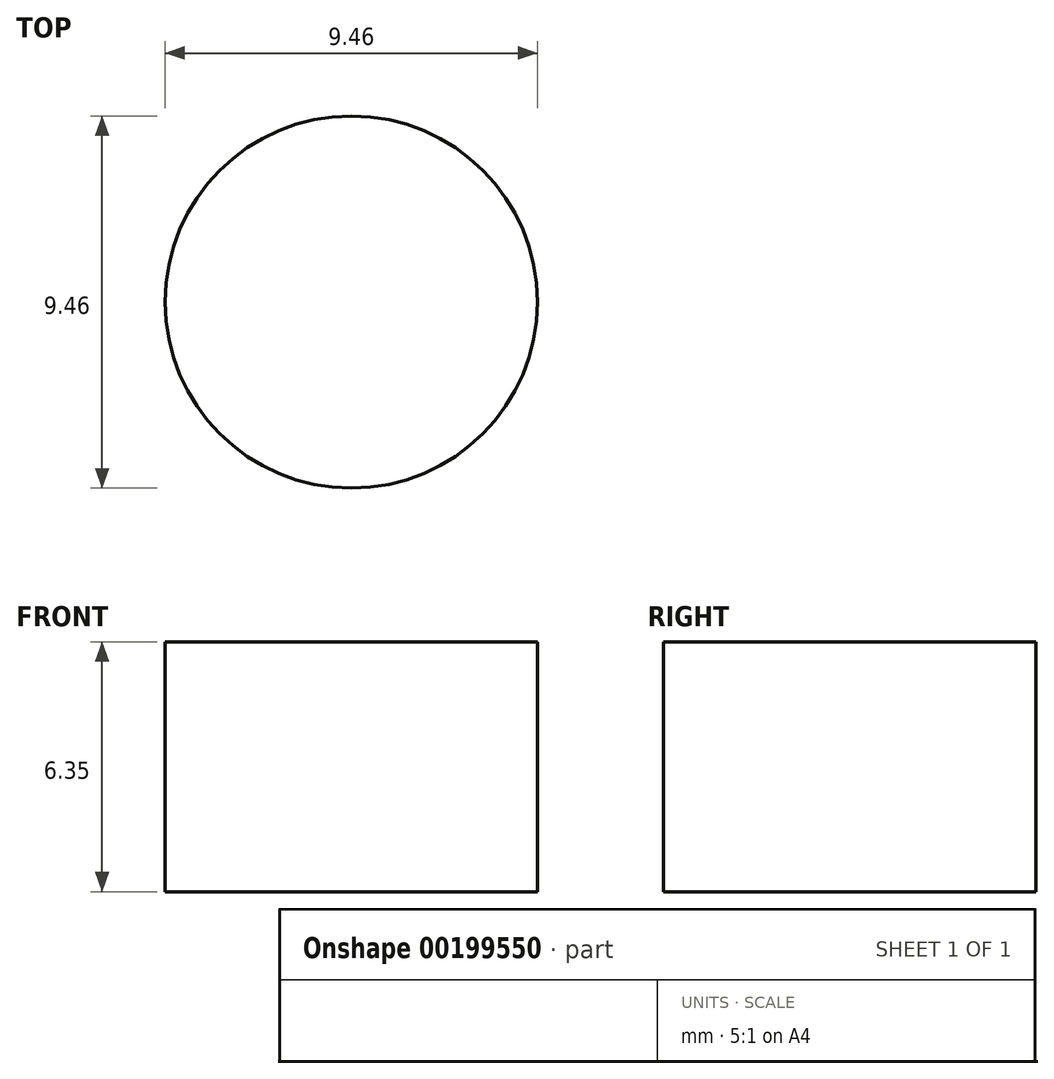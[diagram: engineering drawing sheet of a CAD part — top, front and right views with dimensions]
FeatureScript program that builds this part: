
annotation { "Feature Type Name" : "Feature", "Feature Type Description" : "" }
export const myFeature = defineFeature(function(context is Context, id is Id, definition is map)
    precondition{}
    {
        {
            var Q0;
            Q0=qCreatedBy(makeId("Top.planeOp"),FACE);
            var sketch = newSketch(context, id + "F0", { "sketchPlane" : qUnion([Q0])});
            skCircle(sketch, "E0", {"center": v(0, 0) * mm, "radius": 4.73 * mm});
            skSolve(sketch);
        }
        {
            var Q0;
            Q0 = qSketchRegion(id + "F0", true);
            extrude(context, id + "F1", {"entities" : qUnion([Q0]), "depth" : 6.35 * mm});
        }
    });
